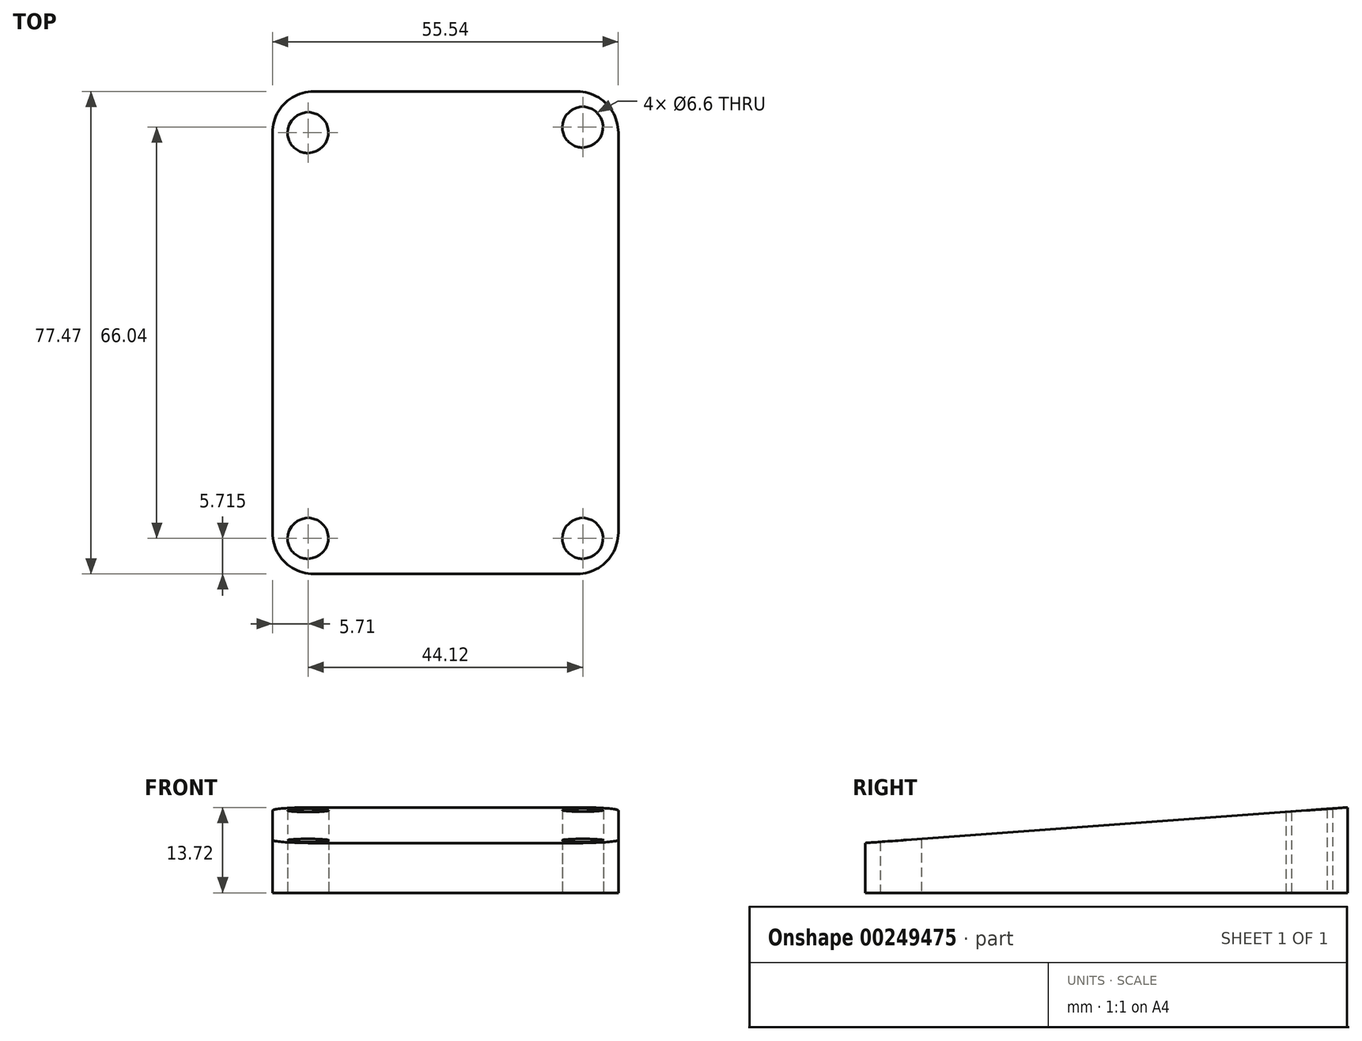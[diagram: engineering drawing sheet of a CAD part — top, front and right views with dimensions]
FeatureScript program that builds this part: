
annotation { "Feature Type Name" : "Feature", "Feature Type Description" : "" }
export const myFeature = defineFeature(function(context is Context, id is Id, definition is map)
    precondition{}
    {
        {
            var Q0;
            Q0=qCreatedBy(makeId("Right.planeOp"),FACE);
            var sketch = newSketch(context, id + "F0", { "sketchPlane" : qUnion([Q0])});
            skLineSegment(sketch, "E0", {"start": v(0, 8) * mm, "end": v(77.47, 13.72) * mm});
            skLineSegment(sketch, "E1", {"start": v(77.47, 13.72) * mm, "end": v(77.47, 0) * mm});
            skLineSegment(sketch, "E2", {"start": v(77.47, 0) * mm, "end": v(0, 0) * mm});
            skLineSegment(sketch, "E3", {"start": v(0, 0) * mm, "end": v(0, 8) * mm});
            skSolve(sketch);
        }
        {
            var Q0;
            Q0 = qSketchRegion(id + "F0", true);
            extrude(context, id + "F1", {"entities" : qUnion([Q0]), "endBound" : BoundingType.SYMMETRIC, "depth" : 55.55 * mm});
        }
        {
            var Q0;
            Q0=makeQuery(id+"F1.opExtrude","CAP_EDGE",EDGE,{"disambiguationData":[OSD([sQuery(id+"F0.wireOp",EDGE,"E3")])],"isStart":false});
            var Q1;
            Q1=makeQuery(id+"F1.opExtrude","CAP_EDGE",EDGE,{"disambiguationData":[OSD([sQuery(id+"F0.wireOp",EDGE,"E1")])],"isStart":false});
            var Q2;
            Q2=makeQuery(id+"F1.opExtrude","CAP_EDGE",EDGE,{"disambiguationData":[OSD([sQuery(id+"F0.wireOp",EDGE,"E1")])],"isStart":true});
            var Q3;
            Q3=makeQuery(id+"F1.opExtrude","CAP_EDGE",EDGE,{"disambiguationData":[OSD([sQuery(id+"F0.wireOp",EDGE,"E3")])],"isStart":true});
            fillet(context, id + "F2", {"entities" : qUnion([Q0, Q1, Q2, Q3]), "radius" : 6.6 * mm, "tangentPropagation" : true, "allowEdgeOverflow" : false});
        }
        {
            var Q0;
            Q0=makeQuery(id+"F1.opExtrude","SWEPT_FACE",FACE,{"disambiguationData":[OSD([sQuery(id+"F0.wireOp",EDGE,"E2")])]});
            var sketch = newSketch(context, id + "F3", { "sketchPlane" : qUnion([Q0])});
            skPoint(sketch, "E4", {"position": v(22.06, -5.71) * mm});
            skPoint(sketch, "E5", {"position": v(22.06, -71.76) * mm});
            skPoint(sketch, "E6", {"position": v(-22.06, -70.87) * mm});
            skPoint(sketch, "E7", {"position": v(-22.06, -5.71) * mm});
            skSolve(sketch);
        }
        {
            var Q0;
            Q0=sQuery(id+"F3.wireOp",VERTEX,"E4");
            var Q1;
            Q1=sQuery(id+"F3.wireOp",VERTEX,"E7");
            var Q2;
            Q2=sQuery(id+"F3.wireOp",VERTEX,"E5");
            var Q3;
            Q3=sQuery(id+"F3.wireOp",VERTEX,"E6");
            var Q4;
            Q4=makeQuery(id+"F1.opExtrude","SWEPT_BODY",BODY,{"disambiguationData":[OSD([sQuery(id+"F0.wireOp",EDGE,"E0"),sQuery(id+"F0.wireOp",EDGE,"E1"),sQuery(id+"F0.wireOp",EDGE,"E2"),sQuery(id+"F0.wireOp",EDGE,"E3")])]});
            hole(context, id + "F4", {"style" : HoleStyle.SIMPLE, "endStyle" : HoleEndStyle.THROUGH, "holeDiameter" : 6.6 * mm, "tappedDepth" : 12.7 * mm, "tapClearance" : 3, "locations" : qUnion([Q0, Q1, Q2, Q3]), "scope" : qUnion([Q4])});
        }
    });
